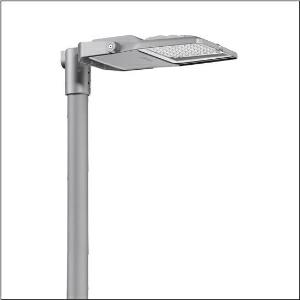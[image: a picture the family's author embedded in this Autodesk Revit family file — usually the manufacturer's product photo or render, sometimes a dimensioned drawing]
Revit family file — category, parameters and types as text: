
# Revit family: floodlight_fl_21_iq_mini___pl61_5xa7772c2c3a_f769
name_source: partatom
category: Lighting Fixtures
units: mm (PartAtom-declared; Revit-internal decimal feet)

## family parameters
Cut with Voids When Loaded = No
Host = Face
Light Source = No
Part Type = Normal
Room Calculation Point = No
Round Connector Dimension = Use Diameter
Shared = No

## types (1)
- --- (1 x LED, 11980 lm, 87.2 W, 3000K)
    Apparent Load = 87 VA
    CIE Flux Codes = 33 65 98 100 100
    Color Rendering = 70
    Color Temperature = 3000K
    Default Elevation = 1800 mm
    Description = Floodlight FL 21 iQ mini, floodlight, primary light control with lens, of PMMA, primary optical cover: protective disc, of toughened safety glass, transparent, light distribution: PL61, light emission: direct distribution, installation type: surface-mounted, LED, High Power LED, rated luminous flux: 11.980lm, luminous efficacy: 137lm/W, light colour: 730, colour temperature: 3000K, control: Auto-Match, Temp-Guard, Night-Set, Smart-Wire, Desk-Remote (wireless, voltage-free reading and setting of iQ features in the workshop via application-optimized NFC function/RFID function), optimised constant luminous flux control (CLO 2.0), Light-Fading, Lumen-Switch, with terminal, 6-pole, mains connection: 220..240V, AC, 50/60Hz, start of lifetime: 87W, end of service life: 92W, reduction: 40W, luminaire housing, of diecast aluminium, powder-coated, Siteco® metallic grey (DB 702S), corrosivity category C5 mid according to DIN EN ISO 12944, sealing non-destructively replaceable, please order mast flange separately, mast bracket, of steel, galvanised, powder-coated, protection rating (complete): IP66, insulation class (complete): insulation class II (safety insulation), certification: CE, ENEC, VDE, protection symbol: D, impact resistance: IK08, permissible operating ambient temperature: -40..+40°C, permissible operating ambient temperature for outdoor applications: -40..+50°C, standard: DIN EN 12944, LABS conformity tested according to VDMA 24364:2018-05, packaging unit: 1 piece

Light Distribution: PL61
    Height = 70 mm
    Lamp = 1 x LED
    Lamp Light Flux = 11980 lm
    Lamp Power = 87.2 W
    Lamp count = 1
    Length = 485 mm
    Luminous efficacy = 137 lm/W
    Manufacturer = Siteco
    ModVariant = No
    Model = 5XA7772C2C3A
    Number of Poles = 1
    OnlyDefault = Yes
    Power Factor = 1
    Product Name = Floodlight FL 21 iQ mini | PL61
    Product group = floodlight | pylon annexe
    ProductGroupID = 6200
    Protection Class = Protection class II
    Protection Degree = IP 66
    RLX_Detail_Level = 1
    RLX_Emergency_Light_Flux = 0 lm
    RLX_Emergency_Type = 0
    RLX_Emergency_Type_DB = No
    RlxData = <blob elided: 101365 chars, md5=4f438db6>
    Socket = socket
    Standby Power = 0 W
    System Light Flux = 11980 lm
    System Power = 87 W
    Type Comments = factory setting: luminous flux: 100 % | dim-lin: 254 | 456 mA
    Type Image = l_1007125.jpg
    URL = http://relux.com
    VarID = @adj_106119
    Voltage = 0 V
    Weight = 0.00 kg
    Width = 337 mm

## geometry (parser evidence)
native form markers: Blend x4, Sweep x12
no freeform markers — native parametric forms only
